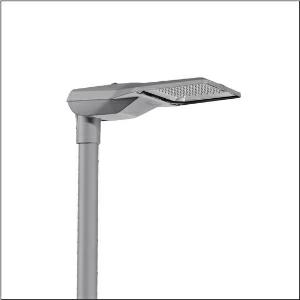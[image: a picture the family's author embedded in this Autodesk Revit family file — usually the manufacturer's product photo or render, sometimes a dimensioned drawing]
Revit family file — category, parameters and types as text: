
# Revit family: streetlight_sl_21_iq_midi___st1_0a_5xe3d31v08nb_ec4a
name_source: partatom
category: Lighting Fixtures
units: mm (PartAtom-declared; Revit-internal decimal feet)

## family parameters
Cut with Voids When Loaded = No
Host = Face
Light Source = No
Part Type = Normal
Room Calculation Point = No
Round Connector Dimension = Use Diameter
Shared = No

## types (1)
- --- (1 x LED, 21550 lm, 136.6 W, 3000K)
    Apparent Load = 137 VA
    CIE Flux Codes = 40 73 97 100 100
    Color Rendering = 70
    Color Temperature = 3000K
    Default Elevation = 1800 mm
    Description = Streetlight SL 21 iQ midi, mast luminaire, primary light control with lens, of PMMA, primary optical cover: cover, of toughened safety glass, transparent, light distribution: ST1.0a, light emission: direct distribution, primary light characteristic: asymmetric, installation type: post-top, side-entry, LED, High Power LED, rated luminous flux: 21.550lm, luminous efficacy: 158lm/W, light colour: 730, colour temperature: 3000K, control: presetting dimming logarithmic, Street-Remote, Auto-Match, Temp-Guard, Lumen-Switch, Night-Set, Smart-Wire, Light-Fading, Desk-Remote (wireless, voltage-free reading and setting of iQ features in the workshop via application-optimized NFC function/RFID function), optimised constant luminous flux control (CLO 2.0), mains connection: 230..240V, AC, 50/60Hz, start of lifetime: 137W, end of service life: 144W, reduction: 61W, luminaire housing, of diecast aluminium, powder-coated, Siteco® metallic grey (DB 702S), corrosivity category C5 mid according to DIN EN ISO 12944, please order mast flange separately, inclination adjustable: 0°, 5°, 10°, 15°, sealing non-destructively replaceable, multi-level sealing system, length: 644mm, width: 335mm, height: 110mm, mast flange for spigot size: 42mm (side-entry): 5XC10008XM4, 60/48mm (side-entry/post-top): 5XC10108XM2, 76/60mm (side-entry/post-top): 5XC10108XM1, Smart Interface above, protection rating (complete): IP66, insulation class (complete): insulation class II (safety insulation), certification: CE, ENEC, ENEC+, VDE, impact resistance: IK09, permissible operating ambient temperature for outdoor applications: -40..+50°C, standard-compliant lighting for roads and squares, packaging unit: 1 piece

Light Distribution: ST1.0a
    Height = 111 mm
    Lamp = 1 x LED
    Lamp Light Flux = 21550 lm
    Lamp Power = 136.6 W
    Lamp count = 1
    Length = 644 mm
    Luminous efficacy = 158 lm/W
    Manufacturer = Siteco
    ModVariant = No
    Model = 5XE3D31V08NB
    Number of Poles = 1
    OnlyDefault = Yes
    Power Factor = 1
    Product Name = Streetlight SL 21 iQ midi | ST1.0a
    Product group = mast luminaire | pylon top
    ProductGroupID = 6100
    Protection Class = Protection class II
    Protection Degree = IP 66
    RLX_Detail_Level = 1
    RLX_Emergency_Light_Flux = 0 lm
    RLX_Emergency_Type = 0
    RLX_Emergency_Type_DB = No
    RlxData = <blob elided: 92369 chars, md5=d6eb27d8>
    Socket = socket
    Standby Power = 0 W
    System Light Flux = 21550 lm
    System Power = 137 W
    Type Comments = factory setting: luminous flux: 100 % | dim-lin: 254 | 733 mA
    Type Image = l_1004302.jpg
    URL = http://relux.com
    VarID = @adj_043959
    Voltage = 0 V
    Weight = 0.00 kg
    Width = 336 mm

## geometry (parser evidence)
native form markers: Blend x4, Sweep x10
no freeform markers — native parametric forms only
